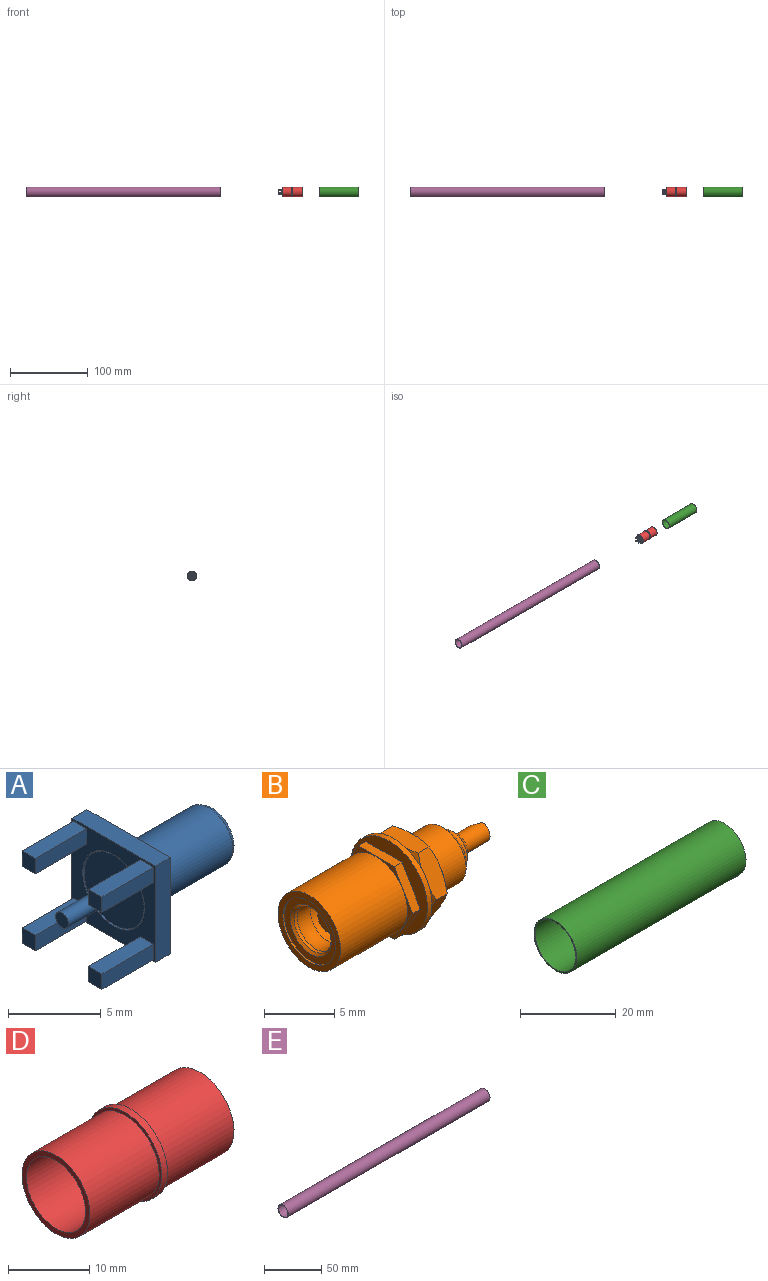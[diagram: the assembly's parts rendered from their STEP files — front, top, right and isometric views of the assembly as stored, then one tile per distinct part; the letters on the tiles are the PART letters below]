
ASSEMBLY  parts=5 mates=4
PART A: 48 faces, bbox 11.4x6.4x6.4 mm
  f0: cylinder r=0.48mm len=3.98mm, axis (1,0,0), area 12.1mm2, adj f46,f47
  f1: cylinder r=2.29mm len=4.57mm, axis (1,0,0), area 2.5mm2, adj f43,f46
  f2: cylinder r=1.52mm len=3.1mm, axis (1,0,0), area 29.7mm2, adj f44,f45
  f3: cone r=1.82mm half-angle=30deg, axis (-1,0,0), area 2.9mm2, adj f4,f44
  f4: cylinder r=1.82mm len=6.12mm, axis (1,0,0), area 69.9mm2, adj f3,f19
  f5: cylinder r=2.35mm len=4.7mm, axis (1,0,0), area 3.1mm2, adj f42,f43
  f6: cone r=1.37mm half-angle=45deg, axis (-1,0,0), area 1.6mm2, adj f7,f16
  f7: cylinder r=1.5mm len=3mm, axis (1,0,0), area 25.9mm2, adj f6,f45
  f8: cylinder r=1.09mm len=3.43mm, axis (1,0,0), area 23.5mm2, adj f14,f16
  f9: torus R=0.41mm, axis (-1,0,0), area 0.3mm2, adj f13,f15
  f10: sphere r=0.15mm, area 0.1mm2, adj f11
  f11: cone r=0.25mm half-angle=15deg, axis (-1,0,0), area 0.5mm2, adj f10,f12
  f12: cylinder r=0.25mm len=2.03mm, axis (1,0,0), area 3.2mm2, adj f11,f15
  f13: cylinder r=0.48mm len=0.97mm, axis (1,0,0), area 0.4mm2, adj f9,f14
  f14: plane 2.18x2.18mm, normal (1,0,0), area 3mm2, adj f8,f13
  f15: plane 0.81x0.81mm, normal (1,0,0), area 0.3mm2, adj f9,f12
  f16: plane 2.74x2.74mm, normal (1,0,0), area 2.2mm2, adj f6,f8
  f17: plane 1.02x1.02mm, normal (-1,0,0), area 1mm2, adj f22,f23,f24,f25
  f18: plane 1.02x1.02mm, normal (-1,0,0), area 1mm2, adj f26,f27,f28,f29
  f19: plane 6.35x6.35mm, normal (1,0,0), area 30mm2, adj f4,f30,f31,f32,f33
  f20: plane 1.02x1.02mm, normal (-1,0,0), area 1mm2, adj f34,f35,f36,f37
  f21: plane 1.02x1.02mm, normal (-1,0,0), area 1mm2, adj f38,f39,f40,f41
  f22: plane 3.94x1.02mm, normal (0,0,1), area 4mm2, adj f17,f23,f25,f42
  f23: plane 3.94x1.02mm, normal (0,1,0), area 4mm2, adj f17,f22,f24,f42
  f24: plane 3.94x1.02mm, normal (0,0,-1), area 4mm2, adj f17,f23,f25,f42
  f25: plane 3.94x1.02mm, normal (0,-1,0), area 4mm2, adj f17,f22,f24,f42
  f26: plane 3.94x1.02mm, normal (0,0,-1), area 4mm2, adj f18,f27,f29,f42
  f27: plane 3.94x1.02mm, normal (0,-1,0), area 4mm2, adj f18,f26,f28,f42
  f28: plane 3.94x1.02mm, normal (0,0,1), area 4mm2, adj f18,f27,f29,f42
  f29: plane 3.94x1.02mm, normal (0,1,0), area 4mm2, adj f18,f26,f28,f42
  f30: plane 6.35x1.14mm, normal (0,0,1), area 7.3mm2, adj f19,f31,f33,f42
  f31: plane 6.35x1.14mm, normal (0,-1,0), area 7.3mm2, adj f19,f30,f32,f42
  f32: plane 6.35x1.14mm, normal (0,0,-1), area 7.3mm2, adj f19,f31,f33,f42
  f33: plane 6.35x1.14mm, normal (0,1,0), area 7.3mm2, adj f19,f30,f32,f42
  f34: plane 3.94x1.02mm, normal (0,-1,0), area 4mm2, adj f20,f35,f37,f42
  f35: plane 3.94x1.02mm, normal (0,0,1), area 4mm2, adj f20,f34,f36,f42
  f36: plane 3.94x1.02mm, normal (0,1,0), area 4mm2, adj f20,f35,f37,f42
  f37: plane 3.94x1.02mm, normal (0,0,-1), area 4mm2, adj f20,f34,f36,f42
  f38: plane 3.94x1.02mm, normal (0,1,0), area 4mm2, adj f21,f39,f41,f42
  f39: plane 3.94x1.02mm, normal (0,0,-1), area 4mm2, adj f21,f38,f40,f42
  f40: plane 3.94x1.02mm, normal (0,-1,0), area 4mm2, adj f21,f39,f41,f42
  f41: plane 3.94x1.02mm, normal (0,0,1), area 4mm2, adj f21,f38,f40,f42
  f42: plane 6.35x6.35mm, normal (-1,0,0), area 18.9mm2, adj f5,f22,f23,f24,f25,f26,f27,f28
  f43: plane 4.7x4.7mm, normal (-1,0,0), area 0.9mm2, adj f1,f5
  f44: plane 3.37x3.37mm, normal (1,0,0), area 1.6mm2, adj f2,f3
  f45: plane 3.05x3.05mm, normal (1,0,0), area 0.2mm2, adj f2,f7
  f46: plane 4.57x4.57mm, normal (-1,0,0), area 15.7mm2, adj f0,f1
  f47: plane 0.97x0.97mm, normal (-1,0,0), area 0.7mm2, adj f0
PART B: 58 faces, bbox 17.8x8x8 mm
  f0: plane 3.18x1.83mm, normal (0,0.87,-0.5), area 2.9mm2, adj f1,f2,f3,f4
  f1: plane 7.33x6.35mm, normal (1,0,0), area 18.1mm2, adj f0,f2,f3,f5,f6,f7,f8,f9
  f2: plane 3.18x1.83mm, normal (0,0.87,0.5), area 2.9mm2, adj f0,f1,f4,f8
  f3: plane 3.67x0.79mm, normal (0,0,-1), area 2.9mm2, adj f0,f1,f4,f5
  f4: plane 7.33x6.35mm, normal (-1,0,0), area 3.8mm2, adj f0,f2,f3,f5,f7,f8,f10
  f5: plane 3.18x1.83mm, normal (0,-0.87,-0.5), area 2.9mm2, adj f1,f3,f4,f7
  f6: plane 2.66x0.51mm, normal (0,1,0), area 1.4mm2, adj f1,f9,f11
  f7: plane 3.18x1.83mm, normal (0,-0.87,0.5), area 2.9mm2, adj f1,f4,f5,f8
  f8: plane 3.67x0.79mm, normal (0,0,1), area 2.9mm2, adj f1,f2,f4,f7
  f9: cylinder r=2.36mm len=4.73mm, axis (-1,0,0), area 6.1mm2, adj f1,f6,f11
  f10: cylinder r=3.15mm len=6.76mm, axis (-1,0,0), area 133.7mm2, adj f4,f12
  f11: plane 7.75x7.75mm, normal (-1,0,0), area 30.3mm2, adj f6,f9,f13
  f12: plane 6.3x6.3mm, normal (-1,0,0), area 9mm2, adj f10,f14
  f13: cylinder r=3.87mm len=7.75mm, axis (-1,0,0), area 11.1mm2, adj f11,f15
  f14: cylinder r=2.65mm len=5.31mm, axis (-1,0,0), area 2.5mm2, adj f12,f16
  f15: plane 7.75x7.75mm, normal (1,0,0), area 30.3mm2, adj f13,f17,f18
  f16: plane 5.31x5.31mm, normal (-1,0,0), area 8.8mm2, adj f14,f19
  f17: cylinder r=2.36mm len=4.73mm, axis (-1,0,0), area 4.6mm2, adj f15,f18,f20
  f18: plane 2.66x0.38mm, normal (0,1,0), area 1mm2, adj f15,f17,f20
  f19: cone r=1.87mm half-angle=45deg, axis (-1,0,0), area 3.3mm2, adj f16,f21
  f20: plane 6.35x6.35mm, normal (-1,0,0), area 14.9mm2, adj f17,f18,f22,f23,f24,f25,f26,f27
  f21: cylinder r=1.87mm len=3.73mm, axis (-1,0,0), area 3.6mm2, adj f19,f28
  f22: cone r=4.45mm half-angle=60deg, axis (1,0,0), area 1mm2, adj f20,f29,f30
  f23: cone r=4.45mm half-angle=60deg, axis (1,0,0), area 1mm2, adj f20,f31,f32
  f24: cone r=4.45mm half-angle=60deg, axis (1,0,0), area 1mm2, adj f20,f32,f33
  f25: cone r=4.45mm half-angle=60deg, axis (1,0,0), area 1mm2, adj f20,f29,f31
  f26: cone r=4.45mm half-angle=60deg, axis (1,0,0), area 1mm2, adj f20,f33,f34
  f27: cone r=4.45mm half-angle=60deg, axis (1,0,0), area 1mm2, adj f20,f30,f34
  f28: torus R=3.3mm, axis (-1,0,0), area 14.9mm2, adj f21,f41
  f29: plane 3.97x1.95mm, normal (0,0,-1), area 5.3mm2, adj f22,f25,f30,f31,f35,f36
  f30: plane 3.48x2.13mm, normal (0,0.87,-0.5), area 5.3mm2, adj f22,f27,f29,f34,f35,f37
  f31: plane 3.48x2.13mm, normal (0,-0.87,-0.5), area 5.3mm2, adj f23,f25,f29,f32,f36,f38
  f32: plane 3.48x2.13mm, normal (0,-0.87,0.5), area 5.3mm2, adj f23,f24,f31,f33,f38,f39
  f33: plane 3.97x1.95mm, normal (0,0,1), area 5.3mm2, adj f24,f26,f32,f34,f39,f40
  f34: plane 3.48x2.13mm, normal (0,0.87,0.5), area 5.3mm2, adj f26,f27,f30,f33,f37,f40
  f35: cone r=3.17mm half-angle=60deg, axis (-1,0,0), area 1mm2, adj f29,f30,f42
  f36: cone r=3.17mm half-angle=60deg, axis (-1,0,0), area 1mm2, adj f29,f31,f42
  f37: cone r=3.17mm half-angle=60deg, axis (-1,0,0), area 1mm2, adj f30,f34,f42
  f38: cone r=3.17mm half-angle=60deg, axis (-1,0,0), area 1mm2, adj f31,f32,f42
  f39: cone r=3.17mm half-angle=60deg, axis (-1,0,0), area 1mm2, adj f32,f33,f42
  f40: cone r=3.17mm half-angle=60deg, axis (-1,0,0), area 1mm2, adj f33,f34,f42
  f41: cylinder r=1.87mm len=3.73mm, axis (-1,0,0), area 31.4mm2, adj f28,f43
  f42: plane 6.35x6.35mm, normal (1,0,0), area 14.9mm2, adj f35,f36,f37,f38,f39,f40,f44,f45
  f43: plane 3.73x3.73mm, normal (-1,0,0), area 7.8mm2, adj f41,f46
  f44: cylinder r=2.36mm len=4.73mm, axis (-1,0,0), area 35.1mm2, adj f42,f45,f47
  f45: plane 3.33x2.66mm, normal (0,1,0), area 8.5mm2, adj f42,f44,f47
  f46: cylinder r=1mm len=2.77mm, axis (-1,0,0), area 17.5mm2, adj f43,f48
  f47: cone r=1.93mm half-angle=45deg, axis (-1,0,0), area 7.2mm2, adj f44,f45,f49
  f48: plane 2.01x2.01mm, normal (-1,0,0), area 3.2mm2, adj f46
  f49: plane 3.86x3.86mm, normal (1,0,0), area 4.3mm2, adj f47,f50
  f50: cylinder r=1.54mm len=3.07mm, axis (-1,0,0), area 5.2mm2, adj f49,f51
  f51: cone r=1.03mm half-angle=45deg, axis (-1,0,0), area 5.8mm2, adj f50,f52
  f52: plane 2.06x2.06mm, normal (1,0,0), area 1.4mm2, adj f51,f53
  f53: cylinder r=0.79mm len=2.51mm, axis (-1,0,0), area 10.6mm2, adj f52,f54,f55
  f54: cylinder r=1.59mm len=1.57mm, axis (0,0,1), area 1.1mm2, adj f53,f55,f56
  f55: plane 1.58x0.83mm, normal (1,0,0), area 0.7mm2, adj f53,f54,f56
  f56: cylinder r=0.44mm len=2.03mm, axis (-1,0,0), area 5mm2, adj f54,f55,f57
  f57: cone r=1732.05mm half-angle=60deg, axis (1,0,0), area 0.7mm2, adj f56
PART C: 4 faces, bbox 50x12.7x12.7 mm
  f0: cylinder r=5.99mm len=50mm, axis (-1,0,0), area 1883.2mm2, adj f2,f3
  f1: cylinder r=6.35mm len=50mm, axis (-1,0,0), area 1994.9mm2, adj f2,f3
  f2: plane 12.7x12.7mm, normal (1,0,0), area 13.8mm2, adj f0,f1
  f3: plane 12.7x12.7mm, normal (-1,0,0), area 13.8mm2, adj f0,f1
PART D: 12 faces, bbox 25x12.7x12.7 mm
  f0: cylinder r=6.35mm len=12.7mm, axis (-1,0,0), area 39.9mm2, adj f1,f2
  f1: plane 12.7x12.7mm, normal (1,0,0), area 17.3mm2, adj f0,f3
  f2: plane 12.7x12.7mm, normal (-1,0,0), area 17.3mm2, adj f0,f5
  f3: cylinder r=5.9mm len=12mm, axis (-1,0,0), area 444.8mm2, adj f1,f4
  f4: plane 11.8x11.8mm, normal (1,0,0), area 23.9mm2, adj f3,f10
  f5: cylinder r=5.9mm len=12mm, axis (1,0,0), area 444.8mm2, adj f2,f6
  f6: plane 11.8x11.8mm, normal (-1,0,0), area 27mm2, adj f5,f7
  f7: cylinder r=5.12mm len=12mm, axis (-1,0,0), area 386mm2, adj f6,f8
  f8: plane 10.24x10.24mm, normal (-1,0,0), area 57mm2, adj f7,f9
  f9: cylinder r=2.84mm len=5.68mm, axis (-1,0,0), area 17.9mm2, adj f8,f11
  f10: cylinder r=5.21mm len=12mm, axis (-1,0,0), area 393.2mm2, adj f4,f11
  f11: plane 10.43x10.43mm, normal (1,0,0), area 60.1mm2, adj f9,f10
PART E: 4 faces, bbox 249x12.7x12.7 mm
  f0: cylinder r=5.99mm len=249mm, axis (-1,0,0), area 9378.3mm2, adj f2,f3
  f1: cylinder r=6.35mm len=249mm, axis (-1,0,0), area 9934.7mm2, adj f2,f3
  f2: plane 12.7x12.7mm, normal (1,0,0), area 13.8mm2, adj f0,f1
  f3: plane 12.7x12.7mm, normal (-1,0,0), area 13.8mm2, adj f0,f1
PLACE A t=(-63.66,-13.19,-22.35)mm
PLACE B t=(-62.03,-13.19,-22.35)mm
PLACE C t=(-19.67,-13.19,-22.35)mm
PLACE D t=(-53.85,-13.19,-22.35)mm
PLACE E t=(-395.42,-13.19,-22.35)mm
MATE slider E.f0 <-> D.f3  axis (-1,0,0) through (-270.92,-13.19,-22.35)mm
MATE slider D.f3 <-> C.f0  axis (-1,0,0) through (-47.35,-13.19,-22.35)mm
MATE fastened B.f9 <-> A.f3  axis (-1,0,0) through (-60.18,-13.19,-22.35)mm
MATE slider B.f9 <-> D.f9  axis (-1,0,0) through (-54.23,-13.19,-22.35)mm
